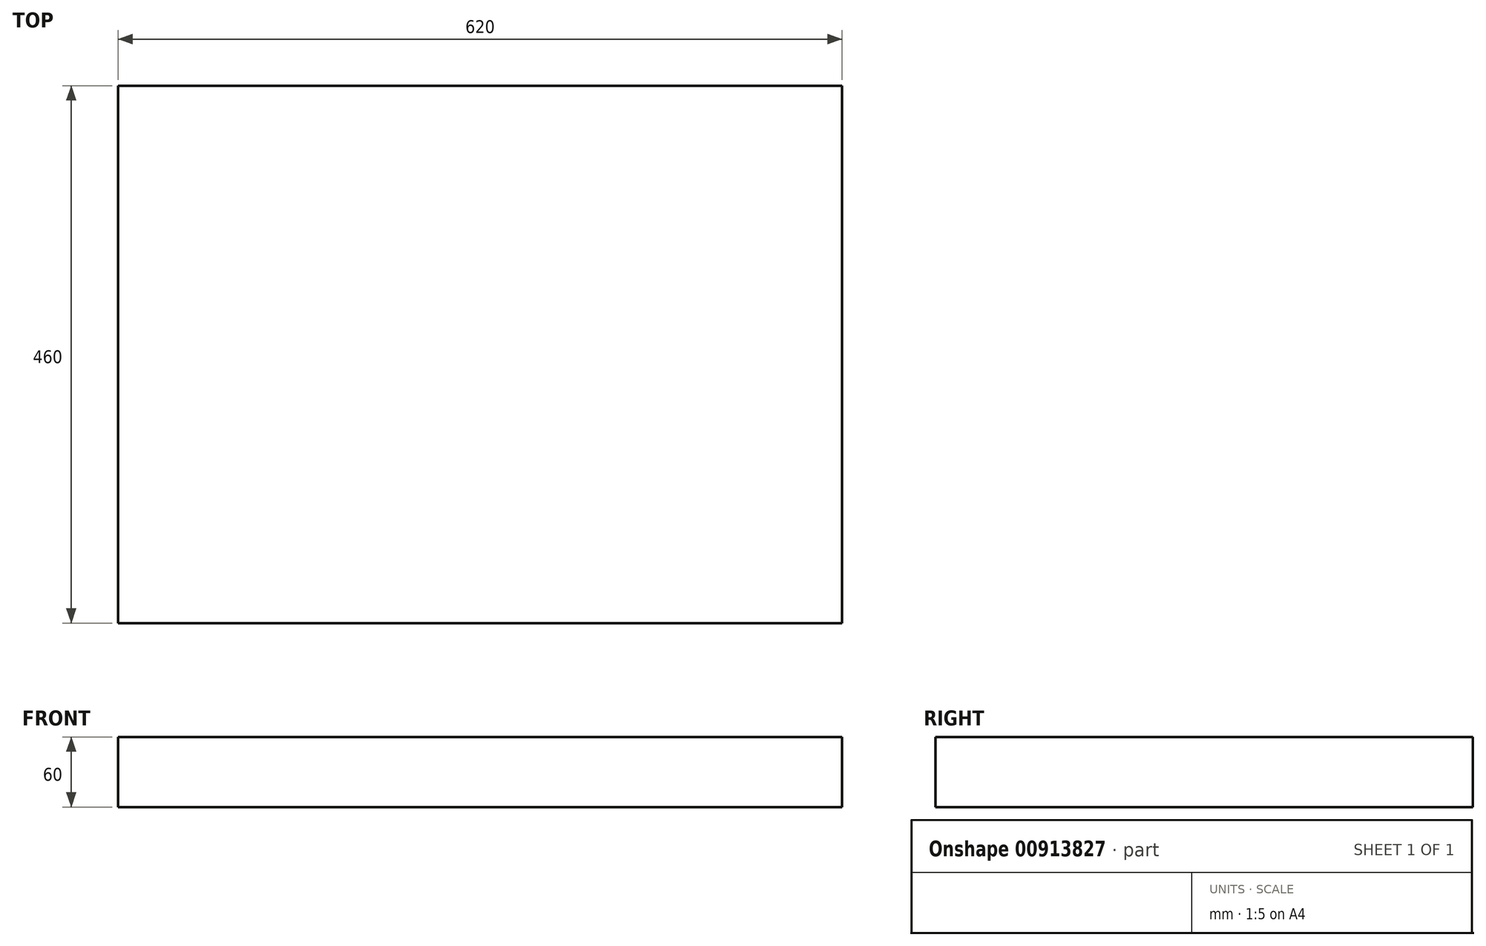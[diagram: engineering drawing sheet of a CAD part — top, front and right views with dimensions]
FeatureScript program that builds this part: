
annotation { "Feature Type Name" : "Feature", "Feature Type Description" : "" }
export const myFeature = defineFeature(function(context is Context, id is Id, definition is map)
    precondition{}
    {
        {
            var Q0;
            Q0=qCreatedBy(makeId("Top.planeOp"),FACE);
            var sketch = newSketch(context, id + "F0", { "sketchPlane" : qUnion([Q0])});
            skLineSegment(sketch, "E0.bottom", {"start": v(310, -230) * mm, "end": v(-310, -230) * mm});
            skLineSegment(sketch, "E0.top", {"start": v(310, 230) * mm, "end": v(-310, 230) * mm});
            skLineSegment(sketch, "E0.left", {"start": v(310, -230) * mm, "end": v(310, 230) * mm});
            skLineSegment(sketch, "E0.right", {"start": v(-310, -230) * mm, "end": v(-310, 230) * mm});
            skPoint(sketch, "E0.middle", {"position": v(0, 0) * mm});
            skLineSegment(sketch, "E1.bottom", {"start": v(320, -240) * mm, "end": v(-320, -240) * mm});
            skLineSegment(sketch, "E1.top", {"start": v(320, 240) * mm, "end": v(-320, 240) * mm});
            skLineSegment(sketch, "E1.left", {"start": v(320, -240) * mm, "end": v(320, 240) * mm});
            skLineSegment(sketch, "E1.right", {"start": v(-320, -240) * mm, "end": v(-320, 240) * mm});
            skSolve(sketch);
        }
        {
            var Q0;
            Q0=makeQuery(id+"F0.imprint","IMPRINT",FACE,{"disambiguationData":[TD([[makeQuery(id+"F0.imprint","IMPRINT",EDGE,{"derivedFrom":sQuery(id+"F0.wireOp",EDGE,"E0.bottom")}),-1.0]])]});
            extrude(context, id + "F1", {"entities" : qUnion([Q0]), "oppositeDirection" : true, "depth" : 60 * mm, "offsetDistance" : 25 * mm});
        }
    });
